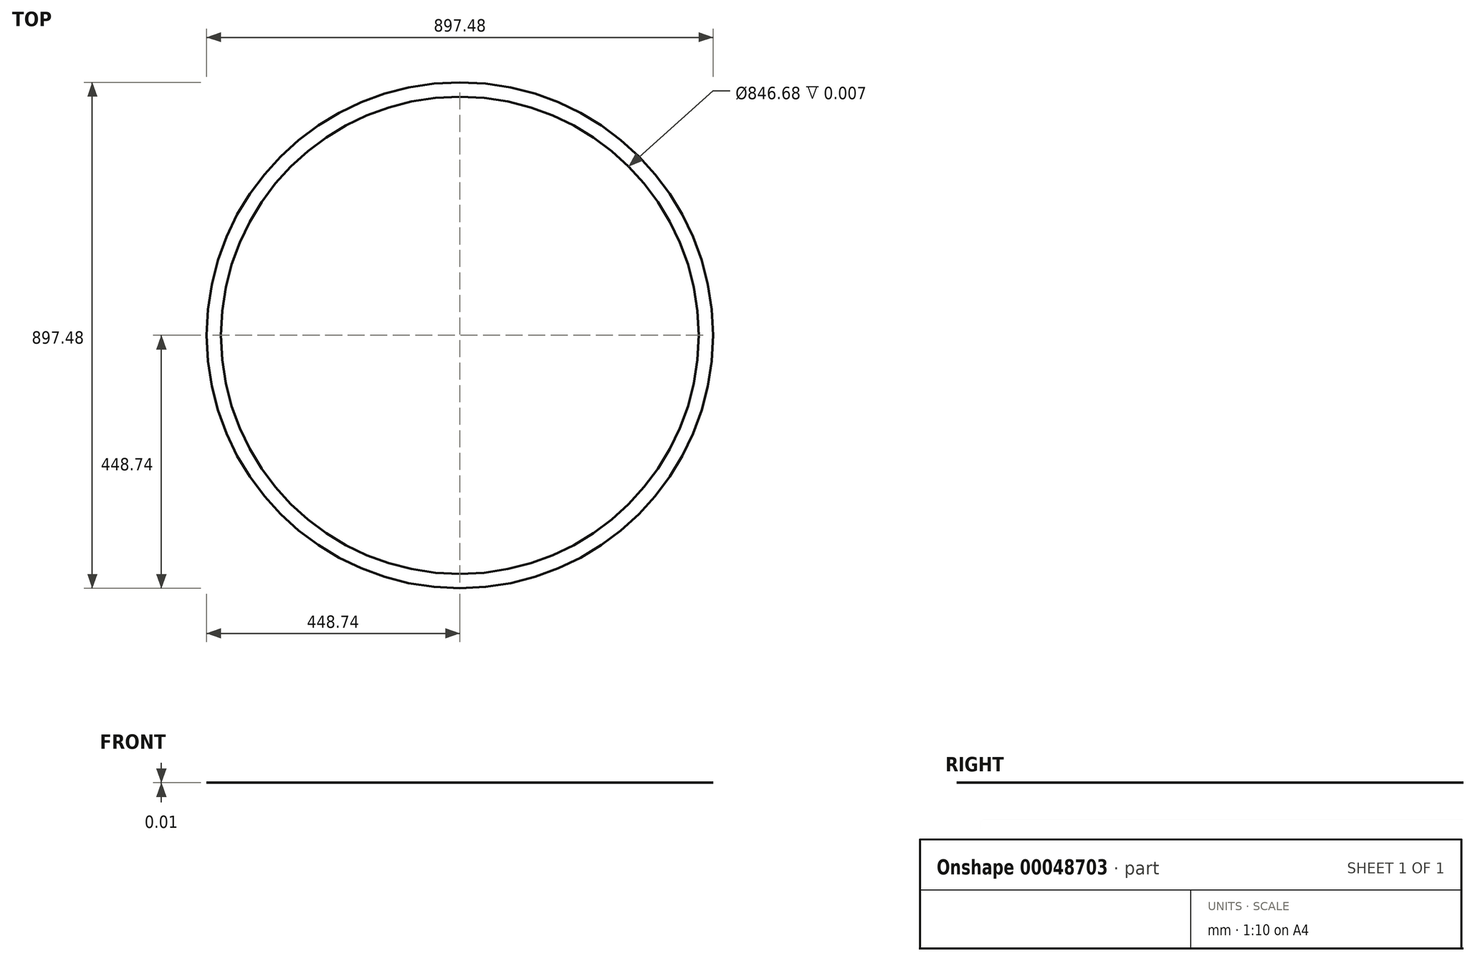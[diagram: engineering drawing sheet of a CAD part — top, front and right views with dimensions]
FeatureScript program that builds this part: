
annotation { "Feature Type Name" : "Feature", "Feature Type Description" : "" }
export const myFeature = defineFeature(function(context is Context, id is Id, definition is map)
    precondition{}
    {
        {
            var Q0;
            Q0=qCreatedBy(makeId("Top.planeOp"),FACE);
            var sketch = newSketch(context, id + "F0", { "sketchPlane" : qUnion([Q0])});
            skCircle(sketch, "E0", {"center": v(0, 0) * mm, "radius": 448.74 * mm});
            skCircle(sketch, "E1", {"center": v(0, 0) * mm, "radius": 423.34 * mm});
            skSolve(sketch);
        }
        {
            var Q0;
            Q0 = qSketchRegion(id + "F0", true);
            extrude(context, id + "F1", {"entities" : qUnion([Q0]), "depth" : 3 / 457.2 * mm});
        }
    });
